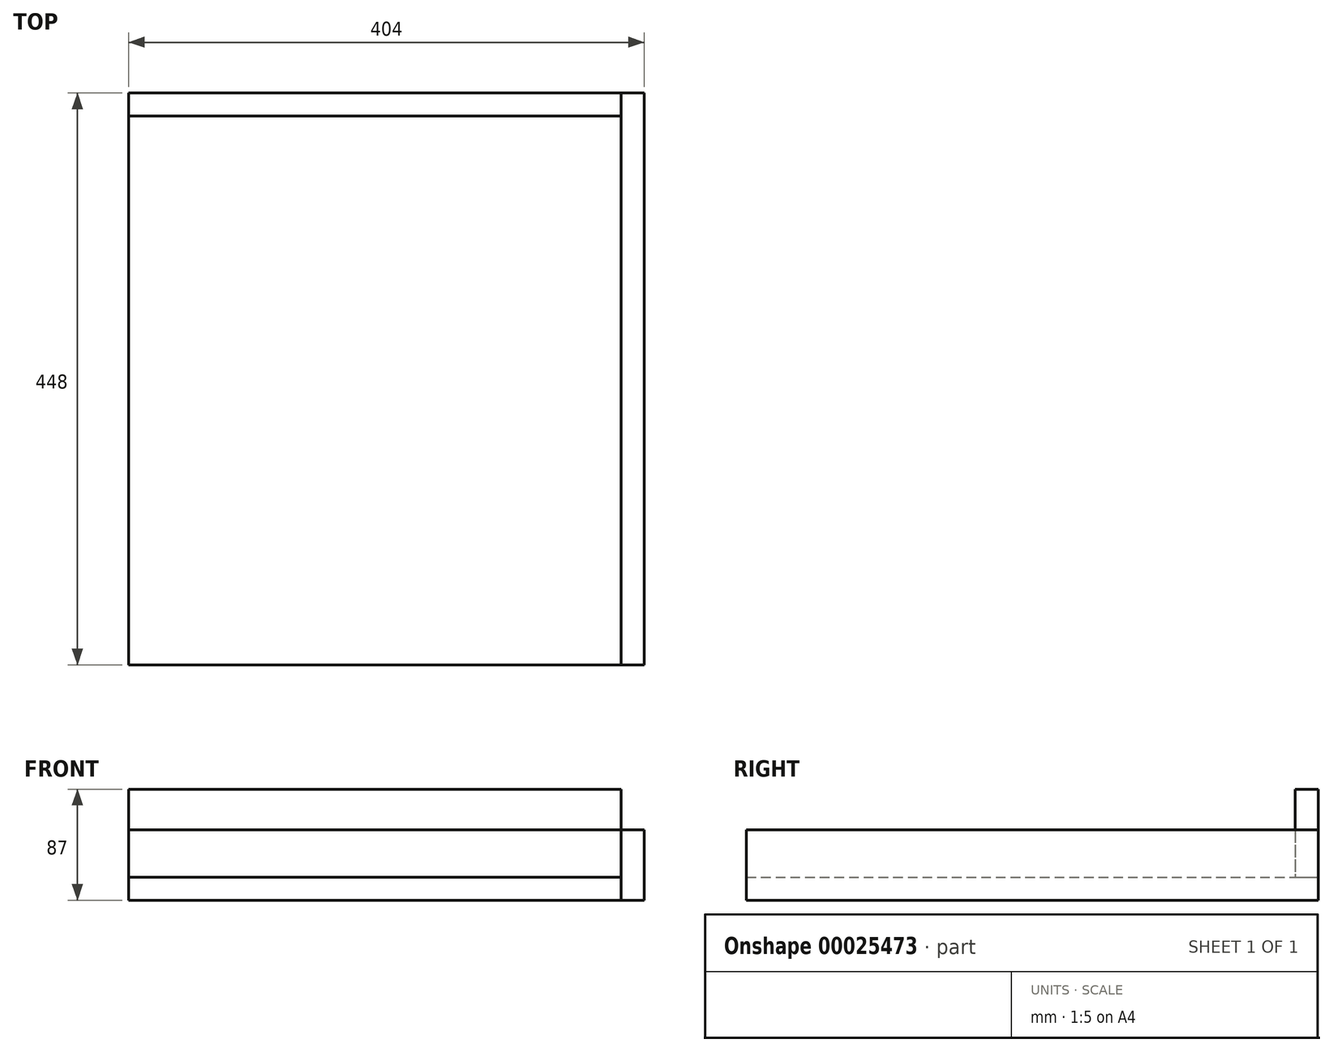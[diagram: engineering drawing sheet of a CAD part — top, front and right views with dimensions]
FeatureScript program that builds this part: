
annotation { "Feature Type Name" : "Feature", "Feature Type Description" : "" }
export const myFeature = defineFeature(function(context is Context, id is Id, definition is map)
    precondition{}
    {
        {
            var Q0;
            Q0=qCreatedBy(makeId("Top.planeOp"),FACE);
            var sketch = newSketch(context, id + "F0", { "sketchPlane" : qUnion([Q0])});
            skLineSegment(sketch, "E0.bottom", {"start": v(-193, 0) * mm, "end": v(193, 0) * mm});
            skLineSegment(sketch, "E0.top", {"start": v(-193, 18) * mm, "end": v(193, 18) * mm});
            skLineSegment(sketch, "E0.left", {"start": v(-193, 0) * mm, "end": v(-193, 18) * mm});
            skLineSegment(sketch, "E0.right", {"start": v(193, 0) * mm, "end": v(193, 18) * mm});
            skSolve(sketch);
        }
        {
            var Q0;
            Q0=makeQuery(id+"F0.imprint","IMPRINT",FACE,{"disambiguationData":[TD([[makeQuery(id+"F0.imprint","IMPRINT",EDGE,{"derivedFrom":sQuery(id+"F0.wireOp",EDGE,"E0.bottom")}),1.0]])]});
            extrude(context, id + "F1", {"entities" : qUnion([Q0]), "depth" : 37 * mm});
        }
        {
            var Q0;
            Q0=makeQuery(id+"F1.opExtrude","SWEPT_FACE",FACE,{"disambiguationData":[OSD([sQuery(id+"F0.wireOp",EDGE,"E0.top")])]});
            var sketch = newSketch(context, id + "F2", { "sketchPlane" : qUnion([Q0])});
            skLineSegment(sketch, "E1.bottom", {"start": v(-193, 0) * mm, "end": v(193, 0) * mm});
            skLineSegment(sketch, "E1.top", {"start": v(-193, -18) * mm, "end": v(193, -18) * mm});
            skLineSegment(sketch, "E1.left", {"start": v(-193, 0) * mm, "end": v(-193, -18) * mm});
            skLineSegment(sketch, "E1.right", {"start": v(193, 0) * mm, "end": v(193, -18) * mm});
            skSolve(sketch);
        }
        {
            var Q0;
            Q0 = qSketchRegion(id + "F2", true);
            extrude(context, id + "F3", {"entities" : qUnion([Q0]), "oppositeDirection" : true, "depth" : 448 * mm});
        }
        {
            var Q0;
            Q0=makeQuery(id+"F3.opExtrude","SWEPT_FACE",FACE,{"disambiguationData":[OSD([sQuery(id+"F2.wireOp",EDGE,"E1.left")])]});
            var sketch = newSketch(context, id + "F4", { "sketchPlane" : qUnion([Q0])});
            skLineSegment(sketch, "E2.bottom", {"start": v(-430, -18) * mm, "end": v(18, -18) * mm});
            skLineSegment(sketch, "E2.top", {"start": v(-430, 37) * mm, "end": v(18, 37) * mm});
            skLineSegment(sketch, "E2.left", {"start": v(-430, -18) * mm, "end": v(-430, 37) * mm});
            skLineSegment(sketch, "E2.right", {"start": v(18, -18) * mm, "end": v(18, 37) * mm});
            skSolve(sketch);
        }
        {
            var Q0;
            Q0 = qSketchRegion(id + "F4", true);
            var Q1;
            {var subQ2=sQuery(id+"F4.wireOp",EDGE,"E2.top");Q1=makeQuery(id+"F4.imprint","IMPRINT",FACE,{"disambiguationData":[TD([[makeQuery(id+"F4.imprint","IMPRINT",EDGE,{"derivedFrom":subQ2}),-1.0]])]});}
            extrude(context, id + "F5", {"entities" : qUnion([Q0, Q1]), "depth" : 18 * mm});
        }
        {
            var Q0;
            Q0 = qSketchRegion(id + "F0", true);
            extrude(context, id + "F6", {"entities" : qUnion([Q0]), "depth" : 69 * mm});
        }
    });
